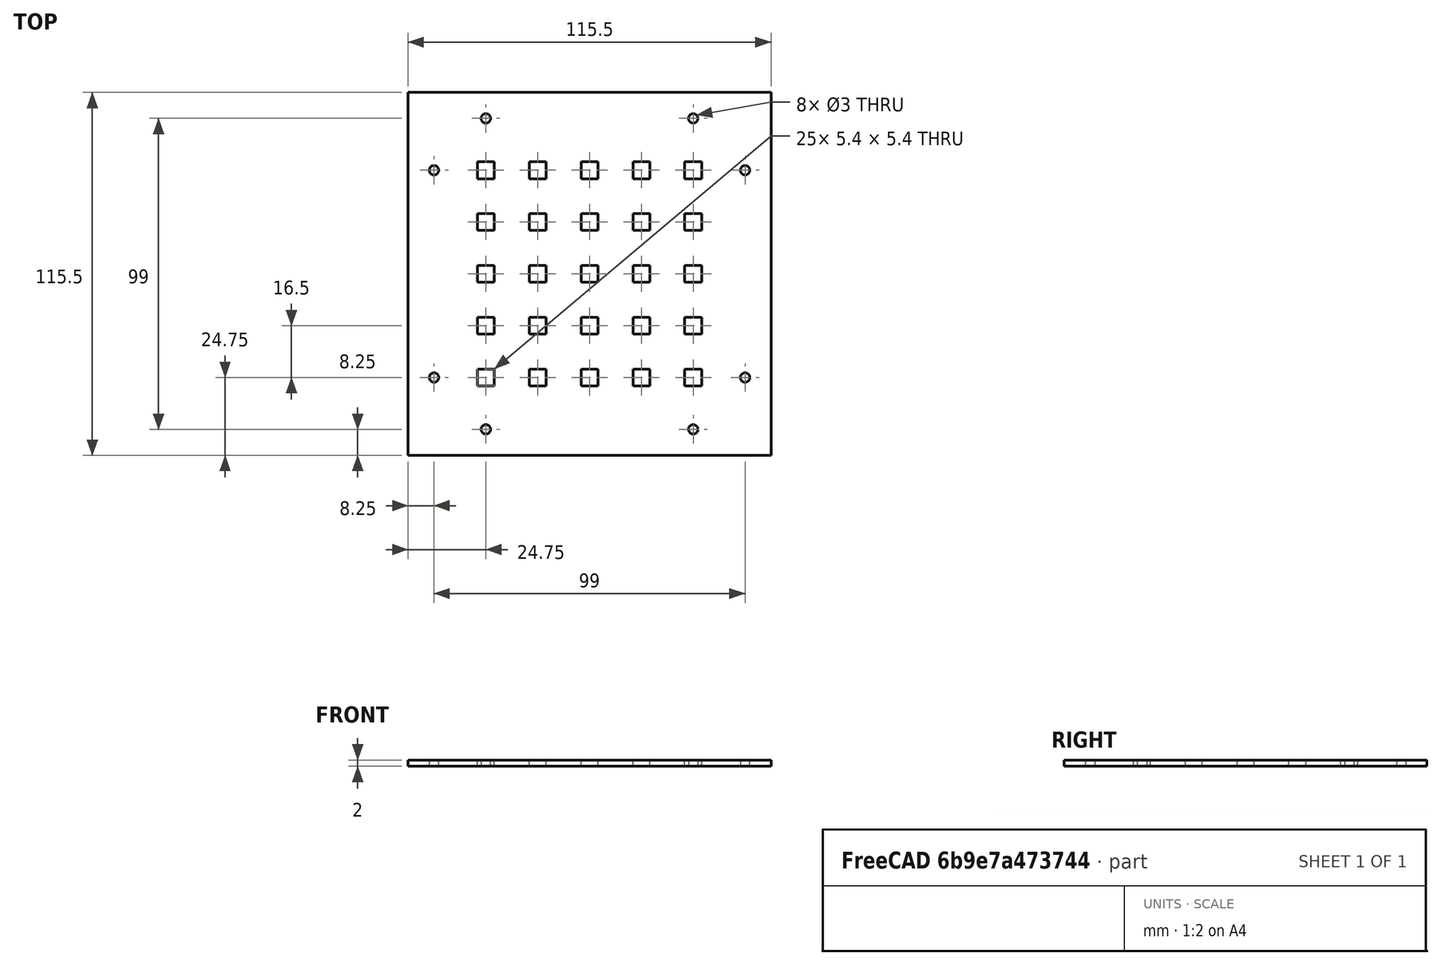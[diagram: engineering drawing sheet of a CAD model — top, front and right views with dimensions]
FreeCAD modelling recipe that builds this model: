
FCSTD DOCUMENT  (FreeCAD 0.21R33771 (Git))
Label: led_matrix_holder_version2
License: All rights reserved
LicenseURL: http://en.wikipedia.org/wiki/All_rights_reserved
objects: Sketcher::SketchObject×1, PartDesign::Pad×1, PartDesign::Body×1
note: 4 computed .brp shape members not serialized (recipe doc carries the construction recipe); baked Part::Feature solids carry a one-line shape summary decoded from their .brp

FEATURE [Sketcher::SketchObject] Sketch
  FullyConstrained = true
  MapMode = 5
  Support = -> [XY_Plane]
  sketch-geometry (142):
    g0: LineSegment StartX=-57.75 StartY=-57.75 StartZ=0 EndX=-57.75 EndY=57.75 EndZ=0
    g1: LineSegment StartX=-57.75 StartY=57.75 StartZ=0 EndX=57.75 EndY=57.75 EndZ=0
    g2: LineSegment StartX=57.75 StartY=57.75 StartZ=0 EndX=57.75 EndY=-57.75 EndZ=0
    g3: LineSegment StartX=57.75 StartY=-57.75 StartZ=0 EndX=-57.75 EndY=-57.75 EndZ=0
    g4: GeomPoint X=0 Y=0 Z=0
    g5: LineSegment StartX=-2.7 StartY=-2.7 StartZ=0 EndX=-2.7 EndY=2.7 EndZ=0
    g6: LineSegment StartX=-2.7 StartY=2.7 StartZ=0 EndX=2.7 EndY=2.7 EndZ=0
    g7: LineSegment StartX=2.7 StartY=2.7 StartZ=0 EndX=2.7 EndY=-2.7 EndZ=0
    g8: LineSegment StartX=2.7 StartY=-2.7 StartZ=0 EndX=-2.7 EndY=-2.7 EndZ=0
    g9: GeomPoint X=0 Y=0 Z=0
    g10: LineSegment StartX=-19.2 StartY=-2.7 StartZ=0 EndX=-19.2 EndY=2.7 EndZ=0
    g11: LineSegment StartX=-19.2 StartY=2.7 StartZ=0 EndX=-13.8 EndY=2.7 EndZ=0
    g12: LineSegment StartX=-13.8 StartY=2.7 StartZ=0 EndX=-13.8 EndY=-2.7 EndZ=0
    g13: LineSegment StartX=-13.8 StartY=-2.7 StartZ=0 EndX=-19.2 EndY=-2.7 EndZ=0
    g14: GeomPoint X=-16.5 Y=0 Z=0
    g15: LineSegment StartX=-35.7 StartY=-2.7 StartZ=0 EndX=-35.7 EndY=2.7 EndZ=0
    g16: LineSegment StartX=-35.7 StartY=2.7 StartZ=0 EndX=-30.3 EndY=2.7 EndZ=0
    g17: LineSegment StartX=-30.3 StartY=2.7 StartZ=0 EndX=-30.3 EndY=-2.7 EndZ=0
    g18: LineSegment StartX=-30.3 StartY=-2.7 StartZ=0 EndX=-35.7 EndY=-2.7 EndZ=0
    g19: GeomPoint X=-33 Y=0 Z=0
    g20: LineSegment StartX=13.8 StartY=-2.7 StartZ=0 EndX=13.8 EndY=2.7 EndZ=0
    g21: LineSegment StartX=13.8 StartY=2.7 StartZ=0 EndX=19.2 EndY=2.7 EndZ=0
    g22: LineSegment StartX=19.2 StartY=2.7 StartZ=0 EndX=19.2 EndY=-2.7 EndZ=0
    g23: LineSegment StartX=19.2 StartY=-2.7 StartZ=0 EndX=13.8 EndY=-2.7 EndZ=0
    g24: GeomPoint X=16.5 Y=0 Z=0
    g25: LineSegment StartX=30.3 StartY=-2.7 StartZ=0 EndX=30.3 EndY=2.7 EndZ=0
    g26: LineSegment StartX=30.3 StartY=2.7 StartZ=0 EndX=35.7 EndY=2.7 EndZ=0
    g27: LineSegment StartX=35.7 StartY=2.7 StartZ=0 EndX=35.7 EndY=-2.7 EndZ=0
    g28: LineSegment StartX=35.7 StartY=-2.7 StartZ=0 EndX=30.3 EndY=-2.7 EndZ=0
    g29: GeomPoint X=33 Y=0 Z=0
    g30: GeomPoint X=-1e-16 Y=-16.5 Z=0
    g31: LineSegment StartX=-2.7 StartY=-19.2 StartZ=0 EndX=-2.7 EndY=-13.8 EndZ=0
    g32: LineSegment StartX=-2.7 StartY=-13.8 StartZ=0 EndX=2.7 EndY=-13.8 EndZ=0
    g33: LineSegment StartX=2.7 StartY=-13.8 StartZ=0 EndX=2.7 EndY=-19.2 EndZ=0
    g34: LineSegment StartX=2.7 StartY=-19.2 StartZ=0 EndX=-2.7 EndY=-19.2 EndZ=0
    g35: GeomPoint X=-1e-16 Y=-16.5 Z=0
    g36: LineSegment StartX=-19.2 StartY=-19.2 StartZ=0 EndX=-19.2 EndY=-13.8 EndZ=0
    g37: LineSegment StartX=-19.2 StartY=-13.8 StartZ=0 EndX=-13.8 EndY=-13.8 EndZ=0
    g38: LineSegment StartX=-13.8 StartY=-13.8 StartZ=0 EndX=-13.8 EndY=-19.2 EndZ=0
    g39: LineSegment StartX=-13.8 StartY=-19.2 StartZ=0 EndX=-19.2 EndY=-19.2 EndZ=0
    g40: GeomPoint X=-16.5 Y=-16.5 Z=0
    g41: LineSegment StartX=-35.7 StartY=-19.2 StartZ=0 EndX=-35.7 EndY=-13.8 EndZ=0
    g42: LineSegment StartX=-35.7 StartY=-13.8 StartZ=0 EndX=-30.3 EndY=-13.8 EndZ=0
    g43: LineSegment StartX=-30.3 StartY=-13.8 StartZ=0 EndX=-30.3 EndY=-19.2 EndZ=0
    g44: LineSegment StartX=-30.3 StartY=-19.2 StartZ=0 EndX=-35.7 EndY=-19.2 EndZ=0
    g45: GeomPoint X=-33 Y=-16.5 Z=0
    g46: LineSegment StartX=13.8 StartY=-19.2 StartZ=0 EndX=13.8 EndY=-13.8 EndZ=0
    g47: LineSegment StartX=13.8 StartY=-13.8 StartZ=0 EndX=19.2 EndY=-13.8 EndZ=0
    g48: LineSegment StartX=19.2 StartY=-13.8 StartZ=0 EndX=19.2 EndY=-19.2 EndZ=0
    g49: LineSegment StartX=19.2 StartY=-19.2 StartZ=0 EndX=13.8 EndY=-19.2 EndZ=0
    g50: GeomPoint X=16.5 Y=-16.5 Z=0
    g51: LineSegment StartX=30.3 StartY=-19.2 StartZ=0 EndX=30.3 EndY=-13.8 EndZ=0
    g52: LineSegment StartX=30.3 StartY=-13.8 StartZ=0 EndX=35.7 EndY=-13.8 EndZ=0
    g53: LineSegment StartX=35.7 StartY=-13.8 StartZ=0 EndX=35.7 EndY=-19.2 EndZ=0
    g54: LineSegment StartX=35.7 StartY=-19.2 StartZ=0 EndX=30.3 EndY=-19.2 EndZ=0
    g55: GeomPoint X=33 Y=-16.5 Z=0
    g56: GeomPoint X=1e-16 Y=16.5 Z=0
    g57: LineSegment StartX=-2.7 StartY=13.8 StartZ=0 EndX=-2.7 EndY=19.2 EndZ=0
    g58: LineSegment StartX=-2.7 StartY=19.2 StartZ=0 EndX=2.7 EndY=19.2 EndZ=0
    g59: LineSegment StartX=2.7 StartY=19.2 StartZ=0 EndX=2.7 EndY=13.8 EndZ=0
    g60: LineSegment StartX=2.7 StartY=13.8 StartZ=0 EndX=-2.7 EndY=13.8 EndZ=0
    g61: GeomPoint X=1e-16 Y=16.5 Z=0
    g62: LineSegment StartX=-19.2 StartY=13.8 StartZ=0 EndX=-19.2 EndY=19.2 EndZ=0
    g63: LineSegment StartX=-19.2 StartY=19.2 StartZ=0 EndX=-13.8 EndY=19.2 EndZ=0
    g64: LineSegment StartX=-13.8 StartY=19.2 StartZ=0 EndX=-13.8 EndY=13.8 EndZ=0
    g65: LineSegment StartX=-13.8 StartY=13.8 StartZ=0 EndX=-19.2 EndY=13.8 EndZ=0
    g66: GeomPoint X=-16.5 Y=16.5 Z=0
    g67: LineSegment StartX=-35.7 StartY=13.8 StartZ=0 EndX=-35.7 EndY=19.2 EndZ=0
    g68: LineSegment StartX=-35.7 StartY=19.2 StartZ=0 EndX=-30.3 EndY=19.2 EndZ=0
    g69: LineSegment StartX=-30.3 StartY=19.2 StartZ=0 EndX=-30.3 EndY=13.8 EndZ=0
    g70: LineSegment StartX=-30.3 StartY=13.8 StartZ=0 EndX=-35.7 EndY=13.8 EndZ=0
    g71: GeomPoint X=-33 Y=16.5 Z=0
    g72: LineSegment StartX=13.8 StartY=13.8 StartZ=0 EndX=13.8 EndY=19.2 EndZ=0
    g73: LineSegment StartX=13.8 StartY=19.2 StartZ=0 EndX=19.2 EndY=19.2 EndZ=0
    g74: LineSegment StartX=19.2 StartY=19.2 StartZ=0 EndX=19.2 EndY=13.8 EndZ=0
    g75: LineSegment StartX=19.2 StartY=13.8 StartZ=0 EndX=13.8 EndY=13.8 EndZ=0
    g76: GeomPoint X=16.5 Y=16.5 Z=0
    g77: LineSegment StartX=30.3 StartY=13.8 StartZ=0 EndX=30.3 EndY=19.2 EndZ=0
    g78: LineSegment StartX=30.3 StartY=19.2 StartZ=0 EndX=35.7 EndY=19.2 EndZ=0
    g79: LineSegment StartX=35.7 StartY=19.2 StartZ=0 EndX=35.7 EndY=13.8 EndZ=0
    g80: LineSegment StartX=35.7 StartY=13.8 StartZ=0 EndX=30.3 EndY=13.8 EndZ=0
    g81: GeomPoint X=33 Y=16.5 Z=0
    g82: GeomPoint X=2e-15 Y=33 Z=0
    g83: LineSegment StartX=-2.7 StartY=30.3 StartZ=0 EndX=-2.7 EndY=35.7 EndZ=0
    g84: LineSegment StartX=-2.7 StartY=35.7 StartZ=0 EndX=2.7 EndY=35.7 EndZ=0
    g85: LineSegment StartX=2.7 StartY=35.7 StartZ=0 EndX=2.7 EndY=30.3 EndZ=0
    g86: LineSegment StartX=2.7 StartY=30.3 StartZ=0 EndX=-2.7 EndY=30.3 EndZ=0
    g87: GeomPoint X=2e-15 Y=33 Z=0
    g88: LineSegment StartX=-19.2 StartY=30.3 StartZ=0 EndX=-19.2 EndY=35.7 EndZ=0
    g89: LineSegment StartX=-19.2 StartY=35.7 StartZ=0 EndX=-13.8 EndY=35.7 EndZ=0
    g90: LineSegment StartX=-13.8 StartY=35.7 StartZ=0 EndX=-13.8 EndY=30.3 EndZ=0
    g91: LineSegment StartX=-13.8 StartY=30.3 StartZ=0 EndX=-19.2 EndY=30.3 EndZ=0
    g92: GeomPoint X=-16.5 Y=33 Z=0
    g93: LineSegment StartX=-35.7 StartY=30.3 StartZ=0 EndX=-35.7 EndY=35.7 EndZ=0
    g94: LineSegment StartX=-35.7 StartY=35.7 StartZ=0 EndX=-30.3 EndY=35.7 EndZ=0
    g95: LineSegment StartX=-30.3 StartY=35.7 StartZ=0 EndX=-30.3 EndY=30.3 EndZ=0
    g96: LineSegment StartX=-30.3 StartY=30.3 StartZ=0 EndX=-35.7 EndY=30.3 EndZ=0
    g97: GeomPoint X=-33 Y=33 Z=0
    g98: LineSegment StartX=13.8 StartY=30.3 StartZ=0 EndX=13.8 EndY=35.7 EndZ=0
    g99: LineSegment StartX=13.8 StartY=35.7 StartZ=0 EndX=19.2 EndY=35.7 EndZ=0
    g100: LineSegment StartX=19.2 StartY=35.7 StartZ=0 EndX=19.2 EndY=30.3 EndZ=0
    g101: LineSegment StartX=19.2 StartY=30.3 StartZ=0 EndX=13.8 EndY=30.3 EndZ=0
    g102: GeomPoint X=16.5 Y=33 Z=0
    g103: LineSegment StartX=30.3 StartY=30.3 StartZ=0 EndX=30.3 EndY=35.7 EndZ=0
    g104: LineSegment StartX=30.3 StartY=35.7 StartZ=0 EndX=35.7 EndY=35.7 EndZ=0
    g105: LineSegment StartX=35.7 StartY=35.7 StartZ=0 EndX=35.7 EndY=30.3 EndZ=0
    g106: LineSegment StartX=35.7 StartY=30.3 StartZ=0 EndX=30.3 EndY=30.3 EndZ=0
    g107: GeomPoint X=33 Y=33 Z=0
    g108: GeomPoint X=-1.7e-15 Y=-33 Z=0
    g109: LineSegment StartX=-2.7 StartY=-35.7 StartZ=0 EndX=-2.7 EndY=-30.3 EndZ=0
    g110: LineSegment StartX=-2.7 StartY=-30.3 StartZ=0 EndX=2.7 EndY=-30.3 EndZ=0
    g111: LineSegment StartX=2.7 StartY=-30.3 StartZ=0 EndX=2.7 EndY=-35.7 EndZ=0
    g112: LineSegment StartX=2.7 StartY=-35.7 StartZ=0 EndX=-2.7 EndY=-35.7 EndZ=0
    g113: GeomPoint X=-1.7e-15 Y=-33 Z=0
    g114: LineSegment StartX=-19.2 StartY=-35.7 StartZ=0 EndX=-19.2 EndY=-30.3 EndZ=0
    g115: LineSegment StartX=-19.2 StartY=-30.3 StartZ=0 EndX=-13.8 EndY=-30.3 EndZ=0
    g116: LineSegment StartX=-13.8 StartY=-30.3 StartZ=0 EndX=-13.8 EndY=-35.7 EndZ=0
    g117: LineSegment StartX=-13.8 StartY=-35.7 StartZ=0 EndX=-19.2 EndY=-35.7 EndZ=0
    g118: GeomPoint X=-16.5 Y=-33 Z=0
    g119: LineSegment StartX=-35.7 StartY=-35.7 StartZ=0 EndX=-35.7 EndY=-30.3 EndZ=0
    g120: LineSegment StartX=-35.7 StartY=-30.3 StartZ=0 EndX=-30.3 EndY=-30.3 EndZ=0
    g121: LineSegment StartX=-30.3 StartY=-30.3 StartZ=0 EndX=-30.3 EndY=-35.7 EndZ=0
    g122: LineSegment StartX=-30.3 StartY=-35.7 StartZ=0 EndX=-35.7 EndY=-35.7 EndZ=0
    g123: GeomPoint X=-33 Y=-33 Z=0
    g124: LineSegment StartX=13.8 StartY=-35.7 StartZ=0 EndX=13.8 EndY=-30.3 EndZ=0
    g125: LineSegment StartX=13.8 StartY=-30.3 StartZ=0 EndX=19.2 EndY=-30.3 EndZ=0
    g126: LineSegment StartX=19.2 StartY=-30.3 StartZ=0 EndX=19.2 EndY=-35.7 EndZ=0
    g127: LineSegment StartX=19.2 StartY=-35.7 StartZ=0 EndX=13.8 EndY=-35.7 EndZ=0
    g128: GeomPoint X=16.5 Y=-33 Z=0
    g129: LineSegment StartX=30.3 StartY=-35.7 StartZ=0 EndX=30.3 EndY=-30.3 EndZ=0
    g130: LineSegment StartX=30.3 StartY=-30.3 StartZ=0 EndX=35.7 EndY=-30.3 EndZ=0
    g131: LineSegment StartX=35.7 StartY=-30.3 StartZ=0 EndX=35.7 EndY=-35.7 EndZ=0
    g132: LineSegment StartX=35.7 StartY=-35.7 StartZ=0 EndX=30.3 EndY=-35.7 EndZ=0
    g133: GeomPoint X=33 Y=-33 Z=0
    g134: Circle CenterX=-49.5 CenterY=33 CenterZ=0 NormalX=0 NormalY=0 NormalZ=1 AngleXU=0 Radius=1.5
    g135: Circle CenterX=-33 CenterY=49.5 CenterZ=0 NormalX=0 NormalY=0 NormalZ=1 AngleXU=0 Radius=1.5
    g136: Circle CenterX=33 CenterY=49.5 CenterZ=0 NormalX=0 NormalY=0 NormalZ=1 AngleXU=0 Radius=1.5
    g137: Circle CenterX=49.5 CenterY=33 CenterZ=0 NormalX=0 NormalY=0 NormalZ=1 AngleXU=0 Radius=1.5
    g138: Circle CenterX=49.5 CenterY=-33 CenterZ=0 NormalX=0 NormalY=0 NormalZ=1 AngleXU=0 Radius=1.5
    g139: Circle CenterX=33 CenterY=-49.5 CenterZ=0 NormalX=0 NormalY=0 NormalZ=1 AngleXU=0 Radius=1.5
    g140: Circle CenterX=-33 CenterY=-49.5 CenterZ=0 NormalX=0 NormalY=0 NormalZ=1 AngleXU=0 Radius=1.5
    g141: Circle CenterX=-49.5 CenterY=-33 CenterZ=0 NormalX=0 NormalY=0 NormalZ=1 AngleXU=0 Radius=1.5
  constraints (364):
    c: Coincident(g0,g1)
    c: Coincident(g1,g2)
    c: Coincident(g2,g3)
    c: Coincident(g3,g0)
    c: Horizontal(g1)
    c: Horizontal(g3)
    c: Vertical(g0)
    c: Vertical(g2)
    c: Symmetric(g1,g0,g4)
    c: Coincident(g4,g-1)
    c: DistanceY(g2,g2) = 115.5
    c: DistanceX(g1,g1) = 115.5
    c: Coincident(g5,g6)
    c: Coincident(g6,g7)
    c: Coincident(g7,g8)
    c: Coincident(g8,g5)
    c: Horizontal(g6)
    c: Horizontal(g8)
    c: Vertical(g5)
    c: Vertical(g7)
    c: Symmetric(g6,g5,g9)
    c: Coincident(g9,g4)
    c: DistanceY(g7,g7) = 5.4
    c: DistanceX(g6,g6) = 5.4
    c: Coincident(g10,g11)
    c: Coincident(g11,g12)
    c: Coincident(g12,g13)
    c: Coincident(g13,g10)
    c: Horizontal(g11)
    c: Horizontal(g13)
    c: Vertical(g10)
    c: Vertical(g12)
    c: Symmetric(g11,g10,g14)
    c: PointOnObject(g14,g-1)
    c: DistanceY(g12,g12) = 5.4
    c: DistanceX(g11,g11) = 5.4
    c: Distance(g14,g4) = 16.5
    c: Coincident(g15,g16)
    c: Coincident(g16,g17)
    c: Coincident(g17,g18)
    c: Coincident(g18,g15)
    c: Horizontal(g16)
    c: Horizontal(g18)
    c: Vertical(g15)
    c: Vertical(g17)
    c: Symmetric(g16,g15,g19)
    c: PointOnObject(g19,g-1)
    c: Coincident(g20,g21)
    c: Coincident(g21,g22)
    c: Coincident(g22,g23)
    c: Coincident(g23,g20)
    c: Horizontal(g21)
    c: Horizontal(g23)
    c: Vertical(g20)
    c: Vertical(g22)
    c: Symmetric(g21,g20,g24)
    c: PointOnObject(g24,g-1)
    c: Coincident(g25,g26)
    c: Coincident(g26,g27)
    c: Coincident(g27,g28)
    c: Coincident(g28,g25)
    c: Horizontal(g26)
    c: Horizontal(g28)
    c: Vertical(g25)
    c: Vertical(g27)
    c: Symmetric(g26,g25,g29)
    c: PointOnObject(g29,g-1)
    c: DistanceX(g16,g16) = 5.4
    c: DistanceY(g17,g17) = 5.4
    c: DistanceX(g21,g21) = 5.4
    c: DistanceX(g26,g26) = 5.4
    c: DistanceY(g22,g22) = 5.4
    c: DistanceY(g27,g27) = 5.4
    c: Distance(g19,g14) = 16.5
    c: Distance(g24,g4) = 16.5
    c: Distance(g29,g24) = 16.5
    c: Coincident(g31,g32)
    c: Coincident(g32,g33)
    c: Coincident(g33,g34)
    c: Coincident(g34,g31)
    c: Horizontal(g32)
    c: Horizontal(g34)
    c: Vertical(g31)
    c: Vertical(g33)
    c: Symmetric(g32,g31,g35)
    c: Coincident(g35,g30)
    c: Equal(g7,g33) = 5.4
    c: Equal(g6,g32) = 5.4
    c: Coincident(g36,g37)
    c: Coincident(g37,g38)
    c: Coincident(g38,g39)
    c: Coincident(g39,g36)
    c: Horizontal(g37)
    c: Horizontal(g39)
    c: Vertical(g36)
    c: Vertical(g38)
    c: Symmetric(g37,g36,g40)
    c: Equal(g12,g38) = 5.4
    c: Equal(g11,g37) = 5.4
    c: Distance(g40,g30) = 16.5
    c: Coincident(g41,g42)
    c: Coincident(g42,g43)
    c: Coincident(g43,g44)
    c: Coincident(g44,g41)
    c: Horizontal(g42)
    c: Horizontal(g44)
    c: Vertical(g41)
    c: Vertical(g43)
    c: Symmetric(g42,g41,g45)
    c: Coincident(g46,g47)
    c: Coincident(g47,g48)
    c: Coincident(g48,g49)
    c: Coincident(g49,g46)
    c: Horizontal(g47)
    c: Horizontal(g49)
    c: Vertical(g46)
    c: Vertical(g48)
    c: Symmetric(g47,g46,g50)
    c: Coincident(g51,g52)
    c: Coincident(g52,g53)
    c: Coincident(g53,g54)
    c: Coincident(g54,g51)
    c: Horizontal(g52)
    c: Horizontal(g54)
    c: Vertical(g51)
    c: Vertical(g53)
    c: Symmetric(g52,g51,g55)
    c: Equal(g16,g42) = 5.4
    c: Equal(g17,g43) = 5.4
    c: Equal(g21,g47) = 5.4
    c: Equal(g26,g52) = 5.4
    c: Equal(g22,g48) = 5.4
    c: Equal(g27,g53) = 5.4
    c: Distance(g45,g40) = 16.5
    c: Distance(g50,g30) = 16.5
    c: Distance(g55,g50) = 16.5
    c: Distance(g32,g-2) = 2.7
    c: Distance(g30,g-1) = 16.5
    c: Distance(g50,g-1) = 16.5
    c: Distance(g55,g-1) = 16.5
    c: Distance(g40,g-1) = 16.5
    c: Distance(g45,g-1) = 16.5
    c: Coincident(g57,g58)
    c: Coincident(g58,g59)
    c: Coincident(g59,g60)
    c: Coincident(g60,g57)
    c: Horizontal(g58)
    c: Horizontal(g60)
    c: Vertical(g57)
    c: Vertical(g59)
    c: Symmetric(g58,g57,g61)
    c: Coincident(g61,g56)
    c: Equal(g7,g59) = 5.4
    c: Equal(g6,g58) = 5.4
    c: Coincident(g62,g63)
    c: Coincident(g63,g64)
    c: Coincident(g64,g65)
    c: Coincident(g65,g62)
    c: Horizontal(g63)
    c: Horizontal(g65)
    c: Vertical(g62)
    c: Vertical(g64)
    c: Symmetric(g63,g62,g66)
    c: Equal(g12,g64) = 5.4
    c: Equal(g11,g63) = 5.4
    c: Distance(g66,g56) = 16.5
    c: Coincident(g67,g68)
    c: Coincident(g68,g69)
    c: Coincident(g69,g70)
    c: Coincident(g70,g67)
    c: Horizontal(g68)
    c: Horizontal(g70)
    c: Vertical(g67)
    c: Vertical(g69)
    c: Symmetric(g68,g67,g71)
    c: Coincident(g72,g73)
    c: Coincident(g73,g74)
    c: Coincident(g74,g75)
    c: Coincident(g75,g72)
    c: Horizontal(g73)
    c: Horizontal(g75)
    c: Vertical(g72)
    c: Vertical(g74)
    c: Symmetric(g73,g72,g76)
    c: Coincident(g77,g78)
    c: Coincident(g78,g79)
    c: Coincident(g79,g80)
    c: Coincident(g80,g77)
    c: Horizontal(g78)
    c: Horizontal(g80)
    c: Vertical(g77)
    c: Vertical(g79)
    c: Symmetric(g78,g77,g81)
    c: Equal(g16,g68) = 5.4
    c: Equal(g17,g69) = 5.4
    c: Equal(g21,g73) = 5.4
    c: Equal(g26,g78) = 5.4
    c: Equal(g22,g74) = 5.4
    c: Equal(g27,g79) = 5.4
    c: Distance(g71,g66) = 16.5
    c: Distance(g76,g56) = 16.5
    c: Distance(g81,g76) = 16.5
    c: Distance(g58,g-2) = 2.7
    c: Distance(g56,g-1) = 16.5
    c: Distance(g76,g-1) = 16.5
    c: Distance(g81,g-1) = 16.5
    c: Distance(g66,g-1) = 16.5
    c: Distance(g71,g-1) = 16.5
    c: Coincident(g83,g84)
    c: Coincident(g84,g85)
    c: Coincident(g85,g86)
    c: Coincident(g86,g83)
    c: Horizontal(g84)
    c: Horizontal(g86)
    c: Vertical(g83)
    c: Vertical(g85)
    c: Symmetric(g84,g83,g87)
    c: Coincident(g87,g82)
    c: Equal(g7,g85) = 5.4
    c: Equal(g6,g84) = 5.4
    c: Coincident(g88,g89)
    c: Coincident(g89,g90)
    c: Coincident(g90,g91)
    c: Coincident(g91,g88)
    c: Horizontal(g89)
    c: Horizontal(g91)
    c: Vertical(g88)
    c: Vertical(g90)
    c: Symmetric(g89,g88,g92)
    c: Equal(g12,g90) = 5.4
    c: Equal(g11,g89) = 5.4
    c: Distance(g92,g82) = 16.5
    c: Coincident(g93,g94)
    c: Coincident(g94,g95)
    c: Coincident(g95,g96)
    c: Coincident(g96,g93)
    c: Horizontal(g94)
    c: Horizontal(g96)
    c: Vertical(g93)
    c: Vertical(g95)
    c: Symmetric(g94,g93,g97)
    c: Coincident(g98,g99)
    c: Coincident(g99,g100)
    c: Coincident(g100,g101)
    c: Coincident(g101,g98)
    c: Horizontal(g99)
    c: Horizontal(g101)
    c: Vertical(g98)
    c: Vertical(g100)
    c: Symmetric(g99,g98,g102)
    c: Coincident(g103,g104)
    c: Coincident(g104,g105)
    c: Coincident(g105,g106)
    c: Coincident(g106,g103)
    c: Horizontal(g104)
    c: Horizontal(g106)
    c: Vertical(g103)
    c: Vertical(g105)
    c: Symmetric(g104,g103,g107)
    c: Equal(g16,g94) = 5.4
    c: Equal(g17,g95) = 5.4
    c: Equal(g21,g99) = 5.4
    c: Equal(g26,g104) = 5.4
    c: Equal(g22,g100) = 5.4
    c: Equal(g27,g105) = 5.4
    c: Distance(g97,g92) = 16.5
    c: Distance(g102,g82) = 16.5
    c: Distance(g107,g102) = 16.5
    c: Distance(g84,g-2) = 2.7
    c: Distance(g82,g56) = 16.5
    c: Distance(g102,g76) = 16.5
    c: Distance(g107,g81) = 16.5
    c: Distance(g92,g66) = 16.5
    c: Distance(g97,g71) = 16.5
    c: Coincident(g109,g110)
    c: Coincident(g110,g111)
    c: Coincident(g111,g112)
    c: Coincident(g112,g109)
    c: Horizontal(g110)
    c: Horizontal(g112)
    c: Vertical(g109)
    c: Vertical(g111)
    c: Symmetric(g110,g109,g113)
    c: Coincident(g113,g108)
    c: Equal(g7,g111) = 5.4
    c: Equal(g6,g110) = 5.4
    c: Coincident(g114,g115)
    c: Coincident(g115,g116)
    c: Coincident(g116,g117)
    c: Coincident(g117,g114)
    c: Horizontal(g115)
    c: Horizontal(g117)
    c: Vertical(g114)
    c: Vertical(g116)
    c: Symmetric(g115,g114,g118)
    c: Equal(g12,g116) = 5.4
    c: Equal(g11,g115) = 5.4
    c: Distance(g118,g108) = 16.5
    c: Coincident(g119,g120)
    c: Coincident(g120,g121)
    c: Coincident(g121,g122)
    c: Coincident(g122,g119)
    c: Horizontal(g120)
    c: Horizontal(g122)
    c: Vertical(g119)
    c: Vertical(g121)
    c: Symmetric(g120,g119,g123)
    c: Coincident(g124,g125)
    c: Coincident(g125,g126)
    c: Coincident(g126,g127)
    c: Coincident(g127,g124)
    c: Horizontal(g125)
    c: Horizontal(g127)
    c: Vertical(g124)
    c: Vertical(g126)
    c: Symmetric(g125,g124,g128)
    c: Coincident(g129,g130)
    c: Coincident(g130,g131)
    c: Coincident(g131,g132)
    c: Coincident(g132,g129)
    c: Horizontal(g130)
    c: Horizontal(g132)
    c: Vertical(g129)
    c: Vertical(g131)
    c: Symmetric(g130,g129,g133)
    c: Equal(g16,g120) = 5.4
    c: Equal(g17,g121) = 5.4
    c: Equal(g21,g125) = 5.4
    c: Equal(g26,g130) = 5.4
    c: Equal(g22,g126) = 5.4
    c: Equal(g27,g131) = 5.4
    c: Distance(g123,g118) = 16.5
    c: Distance(g128,g108) = 16.5
    c: Distance(g133,g128) = 16.5
    c: Distance(g111,g-2) = 2.7
    c: Distance(g108,g30) = 16.5
    c: Distance(g128,g50) = 16.5
    c: Distance(g133,g55) = 16.5
    c: Distance(g118,g40) = 16.5
    c: Distance(g123,g45) = 16.5
    c: Diameter(g134) = 3
    c: Diameter(g135) = 3
    c: Diameter(g136) = 3
    c: Diameter(g137) = 3
    c: Diameter(g138) = 3
    c: Diameter(g139) = 3
    c: Diameter(g140) = 3
    c: Diameter(g141) = 3
    c: Distance(g134,g-1) = 33
    c: Distance(g134,g97) = 16.5
    c: Distance(g135,g-2) = 33
    c: Distance(g135,g97) = 16.5
    c: Distance(g107,g136) = 16.5
    c: Distance(g136,g-2) = 33
    c: Distance(g137,g-1) = 33
    c: Distance(g137,g107) = 16.5
    c: Distance(g141,g-1) = 33
    c: Distance(g141,g123) = 16.5
    c: Distance(g140,g-2) = 33
    c: Distance(g140,g123) = 16.5
    c: Distance(g139,g-2) = 33
    c: Distance(g139,g133) = 16.5
    c: Distance(g138,g-1) = 33
    c: Distance(g138,g133) = 16.5
FEATURE [PartDesign::Pad] Pad
  Direction = (0,0,1)
  Length = 2
  Length2 = 10
  Profile = -> Sketch
  ReferenceAxis = -> Sketch [N_Axis]
  Type = 0
FEATURE [PartDesign::Body] Body
  Group = -> [Sketch,Pad]
  Origin = -> Origin
  Tip = -> Pad
